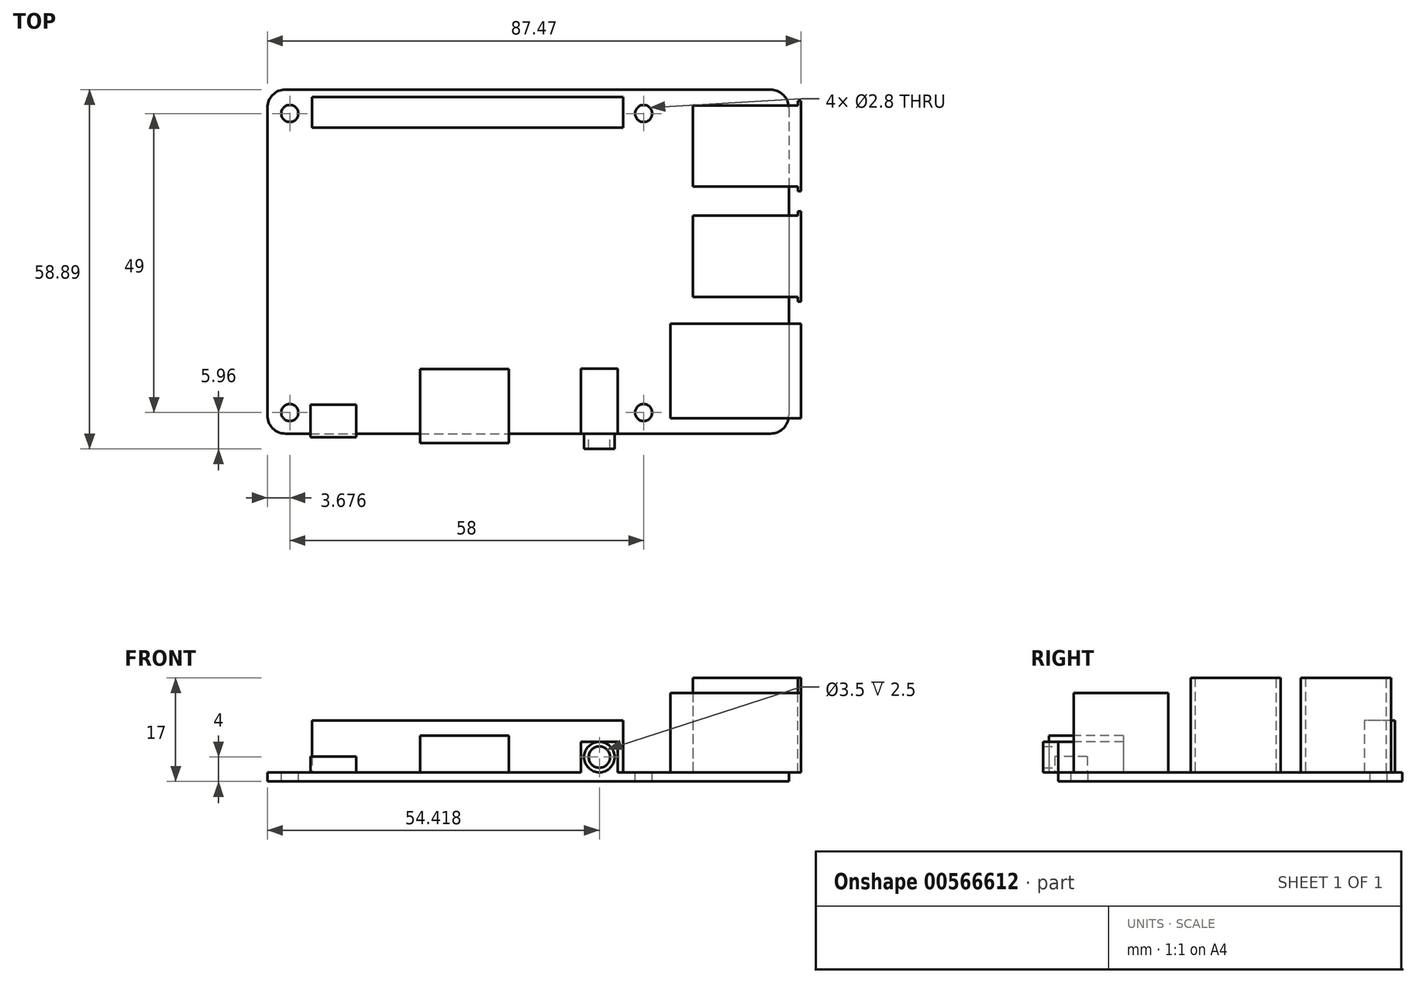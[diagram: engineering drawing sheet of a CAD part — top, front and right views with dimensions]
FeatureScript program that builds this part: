
annotation { "Feature Type Name" : "Feature", "Feature Type Description" : "" }
export const myFeature = defineFeature(function(context is Context, id is Id, definition is map)
    precondition{}
    {
        {
            var Q0;
            Q0=qCreatedBy(makeId("Top.planeOp"),FACE);
            var sketch = newSketch(context, id + "F0", { "sketchPlane" : qUnion([Q0])});
            skLineSegment(sketch, "E0.bottom", {"start": v(17.42, 75.57) * mm, "end": v(102.88, 75.57) * mm});
            skLineSegment(sketch, "E0.top", {"start": v(17.42, 19.18) * mm, "end": v(102.88, 19.18) * mm});
            skLineSegment(sketch, "E0.left", {"start": v(17.42, 75.57) * mm, "end": v(17.42, 19.18) * mm});
            skLineSegment(sketch, "E0.right", {"start": v(102.88, 75.57) * mm, "end": v(102.88, 19.18) * mm});
            skSolve(sketch);
        }
        {
            var Q0;
            Q0 = qSketchRegion(id + "F0", true);
            extrude(context, id + "F1", {"entities" : qUnion([Q0]), "depth" : 1.5 * mm, "offsetDistance" : 25 * mm});
        }
        {
            var Q0;
            Q0=makeQuery(id+"F1.opExtrude","SWEPT_EDGE",EDGE,{"disambiguationData":[OSD([sQuery(id+"F0.wireOp",EDGE,"E0.bottom"),sQuery(id+"F0.wireOp",EDGE,"E0.right")])]});
            var Q1;
            Q1=makeQuery(id+"F1.opExtrude","SWEPT_EDGE",EDGE,{"disambiguationData":[OSD([sQuery(id+"F0.wireOp",EDGE,"E0.bottom"),sQuery(id+"F0.wireOp",EDGE,"E0.left")])]});
            var Q2;
            Q2=makeQuery(id+"F1.opExtrude","SWEPT_EDGE",EDGE,{"disambiguationData":[OSD([sQuery(id+"F0.wireOp",EDGE,"E0.top"),sQuery(id+"F0.wireOp",EDGE,"E0.left")])]});
            var Q3;
            Q3=makeQuery(id+"F1.opExtrude","SWEPT_EDGE",EDGE,{"disambiguationData":[OSD([sQuery(id+"F0.wireOp",EDGE,"E0.top"),sQuery(id+"F0.wireOp",EDGE,"E0.right")])]});
            fillet(context, id + "F2", {"entities" : qUnion([Q0, Q1, Q2, Q3]), "radius" : 3 * mm, "tangentPropagation" : true, "allowEdgeOverflow" : false});
        }
        {
            var Q0;
            Q0=makeQuery(id+"F1.opExtrude","CAP_FACE",FACE,{"disambiguationData":[OSD([sQuery(id+"F0.wireOp",EDGE,"E0.bottom"),sQuery(id+"F0.wireOp",EDGE,"E0.top"),sQuery(id+"F0.wireOp",EDGE,"E0.left"),sQuery(id+"F0.wireOp",EDGE,"E0.right")])],"isStart":false});
            var sketch = newSketch(context, id + "F3", { "sketchPlane" : qUnion([Q0])});
            skLineSegment(sketch, "E1.bottom", {"start": v(24.72, 74.36) * mm, "end": v(75.75, 74.36) * mm});
            skLineSegment(sketch, "E1.top", {"start": v(24.72, 69.31) * mm, "end": v(75.75, 69.31) * mm});
            skLineSegment(sketch, "E1.left", {"start": v(24.72, 74.36) * mm, "end": v(24.72, 69.31) * mm});
            skLineSegment(sketch, "E1.right", {"start": v(75.75, 74.36) * mm, "end": v(75.75, 69.31) * mm});
            skSolve(sketch);
        }
        {
            var Q0;
            Q0 = qSketchRegion(id + "F3", true);
            extrude(context, id + "F4", {"entities" : qUnion([Q0]), "operationType" : NewBodyOperationType.ADD, "depth" : 8.5 * mm, "offsetDistance" : 25 * mm});
        }
        {
            var Q0;
            Q0=makeQuery(id+"F1.opExtrude","CAP_FACE",FACE,{"disambiguationData":[OSD([sQuery(id+"F0.wireOp",EDGE,"E0.bottom"),sQuery(id+"F0.wireOp",EDGE,"E0.top"),sQuery(id+"F0.wireOp",EDGE,"E0.left"),sQuery(id+"F0.wireOp",EDGE,"E0.right")])],"isStart":false});
            var sketch = newSketch(context, id + "F5", { "sketchPlane" : qUnion([Q0])});
            skLineSegment(sketch, "E2.bottom", {"start": v(87.14, 72.94) * mm, "end": v(104.89, 72.94) * mm});
            skLineSegment(sketch, "E2.top", {"start": v(87.14, 59.67) * mm, "end": v(104.89, 59.67) * mm});
            skLineSegment(sketch, "E2.left", {"start": v(87.14, 72.94) * mm, "end": v(87.14, 59.67) * mm});
            skLineSegment(sketch, "E2.right", {"start": v(104.89, 72.94) * mm, "end": v(104.89, 59.67) * mm});
            skLineSegment(sketch, "E3.bottom", {"start": v(87.14, 54.92) * mm, "end": v(104.89, 54.92) * mm});
            skLineSegment(sketch, "E3.top", {"start": v(87.14, 41.58) * mm, "end": v(104.89, 41.58) * mm});
            skLineSegment(sketch, "E3.left", {"start": v(87.14, 54.92) * mm, "end": v(87.14, 41.58) * mm});
            skLineSegment(sketch, "E3.right", {"start": v(104.89, 54.92) * mm, "end": v(104.89, 41.58) * mm});
            skLineSegment(sketch, "E4.bottom", {"start": v(83.45, 37.2) * mm, "end": v(104.89, 37.2) * mm});
            skLineSegment(sketch, "E4.top", {"start": v(83.45, 21.7) * mm, "end": v(104.89, 21.7) * mm});
            skLineSegment(sketch, "E4.left", {"start": v(83.45, 37.2) * mm, "end": v(83.45, 21.7) * mm});
            skLineSegment(sketch, "E4.right", {"start": v(104.89, 37.2) * mm, "end": v(104.89, 21.7) * mm});
            skSolve(sketch);
        }
        {
            var Q0;
            {var subQ0=sQuery(id+"F5.wireOp",EDGE,"E3.right");Q0=makeQuery(id+"F5.imprint","IMPRINT",FACE,{"disambiguationData":[TD([[makeQuery(id+"F5.imprint","IMPRINT",EDGE,{"derivedFrom":subQ0}),-1.0]])]});}
            var Q1;
            {var subQ0=sQuery(id+"F5.wireOp",EDGE,"E3.left");Q1=makeQuery(id+"F5.imprint","IMPRINT",FACE,{"disambiguationData":[TD([[makeQuery(id+"F5.imprint","IMPRINT",EDGE,{"derivedFrom":subQ0}),1.0]])]});}
            var Q2;
            {var subQ0=sQuery(id+"F5.wireOp",EDGE,"E2.right");Q2=makeQuery(id+"F5.imprint","IMPRINT",FACE,{"disambiguationData":[TD([[makeQuery(id+"F5.imprint","IMPRINT",EDGE,{"derivedFrom":subQ0}),-1.0]])]});}
            var Q3;
            {var subQ7=sQuery(id+"F5.wireOp",EDGE,"E2.left");Q3=makeQuery(id+"F5.imprint","IMPRINT",FACE,{"disambiguationData":[TD([[makeQuery(id+"F5.imprint","IMPRINT",EDGE,{"derivedFrom":subQ7}),1.0]])]});}
            extrude(context, id + "F6", {"entities" : qUnion([Q0, Q1, Q2, Q3]), "operationType" : NewBodyOperationType.ADD, "depth" : 15.5 * mm, "offsetDistance" : 25 * mm});
        }
        {
            var Q0;
            {var subQ7=sQuery(id+"F5.wireOp",EDGE,"E4.left");Q0=makeQuery(id+"F5.imprint","IMPRINT",FACE,{"disambiguationData":[TD([[makeQuery(id+"F5.imprint","IMPRINT",EDGE,{"derivedFrom":subQ7}),1.0]])]});}
            var Q1;
            {var subQ0=sQuery(id+"F5.wireOp",EDGE,"E4.right");Q1=makeQuery(id+"F5.imprint","IMPRINT",FACE,{"disambiguationData":[TD([[makeQuery(id+"F5.imprint","IMPRINT",EDGE,{"derivedFrom":subQ0}),-1.0]])]});}
            extrude(context, id + "F7", {"entities" : qUnion([Q0, Q1]), "operationType" : NewBodyOperationType.ADD, "depth" : 13 * mm, "offsetDistance" : 25 * mm});
        }
        {
            var Q0;
            Q0=makeQuery(id+"F6.opExtrude","CAP_FACE",FACE,{"disambiguationData":[OSD([sQuery(id+"F5.wireOp",EDGE,"E2.bottom"),sQuery(id+"F5.wireOp",EDGE,"E2.top"),sQuery(id+"F5.wireOp",EDGE,"E2.left"),sQuery(id+"F5.wireOp",EDGE,"E2.right")])],"isStart":false});
            var sketch = newSketch(context, id + "F8", { "sketchPlane" : qUnion([Q0])});
            skLineSegment(sketch, "E5.bottom", {"start": v(104.4, 73.7) * mm, "end": v(104.89, 73.7) * mm});
            skLineSegment(sketch, "E5.top", {"start": v(104.4, 58.9) * mm, "end": v(104.89, 58.9) * mm});
            skLineSegment(sketch, "E5.left", {"start": v(104.4, 73.7) * mm, "end": v(104.4, 58.9) * mm});
            skLineSegment(sketch, "E5.right", {"start": v(104.89, 73.7) * mm, "end": v(104.89, 58.9) * mm});
            skLineSegment(sketch, "E6.bottom", {"start": v(104.4, 55.63) * mm, "end": v(104.89, 55.63) * mm});
            skLineSegment(sketch, "E6.top", {"start": v(104.4, 40.84) * mm, "end": v(104.89, 40.84) * mm});
            skLineSegment(sketch, "E6.left", {"start": v(104.4, 55.63) * mm, "end": v(104.4, 40.84) * mm});
            skLineSegment(sketch, "E6.right", {"start": v(104.89, 55.63) * mm, "end": v(104.89, 40.84) * mm});
            skSolve(sketch);
        }
        {
            var Q0;
            Q0 = qSketchRegion(id + "F8", true);
            extrude(context, id + "F9", {"entities" : qUnion([Q0]), "operationType" : NewBodyOperationType.ADD, "oppositeDirection" : true, "depth" : 15.5 * mm, "offsetDistance" : 25 * mm});
        }
        {
            var Q0;
            Q0=makeQuery(id+"F1.opExtrude","CAP_FACE",FACE,{"disambiguationData":[OSD([sQuery(id+"F0.wireOp",EDGE,"E0.bottom"),sQuery(id+"F0.wireOp",EDGE,"E0.top"),sQuery(id+"F0.wireOp",EDGE,"E0.left"),sQuery(id+"F0.wireOp",EDGE,"E0.right")])],"isStart":false});
            var sketch = newSketch(context, id + "F10", { "sketchPlane" : qUnion([Q0])});
            skLineSegment(sketch, "E7.bottom", {"start": v(42.44, 29.8) * mm, "end": v(57, 29.8) * mm});
            skLineSegment(sketch, "E7.top", {"start": v(42.44, 17.65) * mm, "end": v(57, 17.65) * mm});
            skLineSegment(sketch, "E7.left", {"start": v(42.44, 29.8) * mm, "end": v(42.44, 17.65) * mm});
            skLineSegment(sketch, "E7.right", {"start": v(57, 29.8) * mm, "end": v(57, 17.65) * mm});
            skSolve(sketch);
        }
        {
            var Q0;
            Q0 = qSketchRegion(id + "F10", true);
            extrude(context, id + "F11", {"entities" : qUnion([Q0]), "operationType" : NewBodyOperationType.ADD, "depth" : 6 * mm, "offsetDistance" : 25 * mm});
        }
        {
            var Q0;
            Q0=makeQuery(id+"F1.opExtrude","CAP_FACE",FACE,{"disambiguationData":[OSD([sQuery(id+"F0.wireOp",EDGE,"E0.bottom"),sQuery(id+"F0.wireOp",EDGE,"E0.top"),sQuery(id+"F0.wireOp",EDGE,"E0.left"),sQuery(id+"F0.wireOp",EDGE,"E0.right")])],"isStart":false});
            var sketch = newSketch(context, id + "F12", { "sketchPlane" : qUnion([Q0])});
            skLineSegment(sketch, "E8.bottom", {"start": v(68.84, 29.85) * mm, "end": v(74.84, 29.85) * mm});
            skLineSegment(sketch, "E8.top", {"start": v(68.84, 19.18) * mm, "end": v(74.84, 19.18) * mm});
            skLineSegment(sketch, "E8.left", {"start": v(68.84, 29.85) * mm, "end": v(68.84, 19.18) * mm});
            skLineSegment(sketch, "E8.right", {"start": v(74.84, 29.85) * mm, "end": v(74.84, 19.18) * mm});
            skSolve(sketch);
        }
        {
            var Q0;
            Q0 = qSketchRegion(id + "F12", true);
            extrude(context, id + "F13", {"entities" : qUnion([Q0]), "operationType" : NewBodyOperationType.ADD, "depth" : 5 * mm, "offsetDistance" : 25 * mm});
        }
        {
            var Q0;
            Q0=makeQuery(id+"F13.boolean.opBoolean","MERGE",FACE,{"derivedFrom":[makeQuery(id+"F1.opExtrude","SWEPT_FACE",FACE,{"disambiguationData":[OSD([sQuery(id+"F0.wireOp",EDGE,"E0.top")])]}),makeQuery(id+"F13.opExtrude","SWEPT_FACE",FACE,{"disambiguationData":[OSD([sQuery(id+"F12.wireOp",EDGE,"E8.top")])]})]});
            var sketch = newSketch(context, id + "F14", { "sketchPlane" : qUnion([Q0])});
            skPoint(sketch, "E9", {"position": v(71.84, 4) * mm});
            skPoint(sketch, "E10.orphan", {"position": v(74.84, 6.5) * mm});
            skPoint(sketch, "E11.end.orphan", {"position": v(68.84, 1.5) * mm});
            skCircle(sketch, "E12", {"center": v(71.84, 4) * mm, "radius": 2.5 * mm});
            skCircle(sketch, "E13", {"center": v(71.84, 4) * mm, "radius": 1.75 * mm});
            skSolve(sketch);
        }
        {
            var Q0;
            Q0=makeQuery(id+"F14.imprint","IMPRINT",FACE,{"disambiguationData":[TD([[makeQuery(id+"F14.imprint","IMPRINT",EDGE,{"derivedFrom":sQuery(id+"F14.wireOp",EDGE,"E12")}),1.0]])]});
            extrude(context, id + "F15", {"entities" : qUnion([Q0]), "operationType" : NewBodyOperationType.ADD, "depth" : 2.5 * mm, "offsetDistance" : 25 * mm});
        }
        {
            var Q0;
            Q0=makeQuery(id+"F1.opExtrude","CAP_FACE",FACE,{"disambiguationData":[OSD([sQuery(id+"F0.wireOp",EDGE,"E0.bottom"),sQuery(id+"F0.wireOp",EDGE,"E0.top"),sQuery(id+"F0.wireOp",EDGE,"E0.left"),sQuery(id+"F0.wireOp",EDGE,"E0.right")])],"isStart":false});
            var sketch = newSketch(context, id + "F16", { "sketchPlane" : qUnion([Q0])});
            skLineSegment(sketch, "E14.bottom", {"start": v(24.48, 23.9) * mm, "end": v(32, 23.9) * mm});
            skLineSegment(sketch, "E14.top", {"start": v(24.48, 18.57) * mm, "end": v(32, 18.57) * mm});
            skLineSegment(sketch, "E14.left", {"start": v(24.48, 23.9) * mm, "end": v(24.48, 18.57) * mm});
            skLineSegment(sketch, "E14.right", {"start": v(32, 23.9) * mm, "end": v(32, 18.57) * mm});
            skSolve(sketch);
        }
        {
            var Q0;
            Q0 = qSketchRegion(id + "F16", true);
            extrude(context, id + "F17", {"entities" : qUnion([Q0]), "operationType" : NewBodyOperationType.ADD, "depth" : 2.6 * mm, "offsetDistance" : 25 * mm});
        }
        {
            var Q0;
            Q0=makeQuery(id+"F1.opExtrude","CAP_FACE",FACE,{"disambiguationData":[OSD([sQuery(id+"F0.wireOp",EDGE,"E0.bottom"),sQuery(id+"F0.wireOp",EDGE,"E0.top"),sQuery(id+"F0.wireOp",EDGE,"E0.left"),sQuery(id+"F0.wireOp",EDGE,"E0.right")])],"isStart":false});
            var sketch = newSketch(context, id + "F18", { "sketchPlane" : qUnion([Q0])});
            skCircle(sketch, "E15", {"center": v(21.1, 71.64) * mm, "radius": 1.4 * mm});
            skCircle(sketch, "E16", {"center": v(79.1, 71.64) * mm, "radius": 1.4 * mm});
            skCircle(sketch, "E17", {"center": v(21.1, 22.64) * mm, "radius": 1.4 * mm});
            skCircle(sketch, "E18", {"center": v(79.1, 22.64) * mm, "radius": 1.4 * mm});
            skCircle(sketch, "E19", {"center": v(79.1, 22.64) * mm, "radius": 3.1 * mm});
            skCircle(sketch, "E20", {"center": v(21.1, 22.64) * mm, "radius": 3.1 * mm});
            skCircle(sketch, "E21", {"center": v(21.1, 71.64) * mm, "radius": 3.1 * mm});
            skCircle(sketch, "E22", {"center": v(79.1, 71.64) * mm, "radius": 3.1 * mm});
            skSolve(sketch);
        }
        {
            var Q0;
            Q0=makeQuery(id+"F18.imprint","IMPRINT",FACE,{"disambiguationData":[TD([[makeQuery(id+"F18.imprint","IMPRINT",EDGE,{"derivedFrom":sQuery(id+"F18.wireOp",EDGE,"E16")}),1.0]])]});
            var Q1;
            Q1=makeQuery(id+"F18.imprint","IMPRINT",FACE,{"disambiguationData":[TD([[makeQuery(id+"F18.imprint","IMPRINT",EDGE,{"derivedFrom":sQuery(id+"F18.wireOp",EDGE,"E18")}),1.0]])]});
            var Q2;
            Q2=makeQuery(id+"F18.imprint","IMPRINT",FACE,{"disambiguationData":[TD([[makeQuery(id+"F18.imprint","IMPRINT",EDGE,{"derivedFrom":sQuery(id+"F18.wireOp",EDGE,"E17")}),1.0]])]});
            var Q3;
            Q3=makeQuery(id+"F18.imprint","IMPRINT",FACE,{"disambiguationData":[TD([[makeQuery(id+"F18.imprint","IMPRINT",EDGE,{"derivedFrom":sQuery(id+"F18.wireOp",EDGE,"E15")}),1.0]])]});
            extrude(context, id + "F19", {"entities" : qUnion([Q0, Q1, Q2, Q3]), "operationType" : NewBodyOperationType.REMOVE, "oppositeDirection" : true, "depth" : 25 * mm, "offsetDistance" : 25 * mm});
        }
    });
